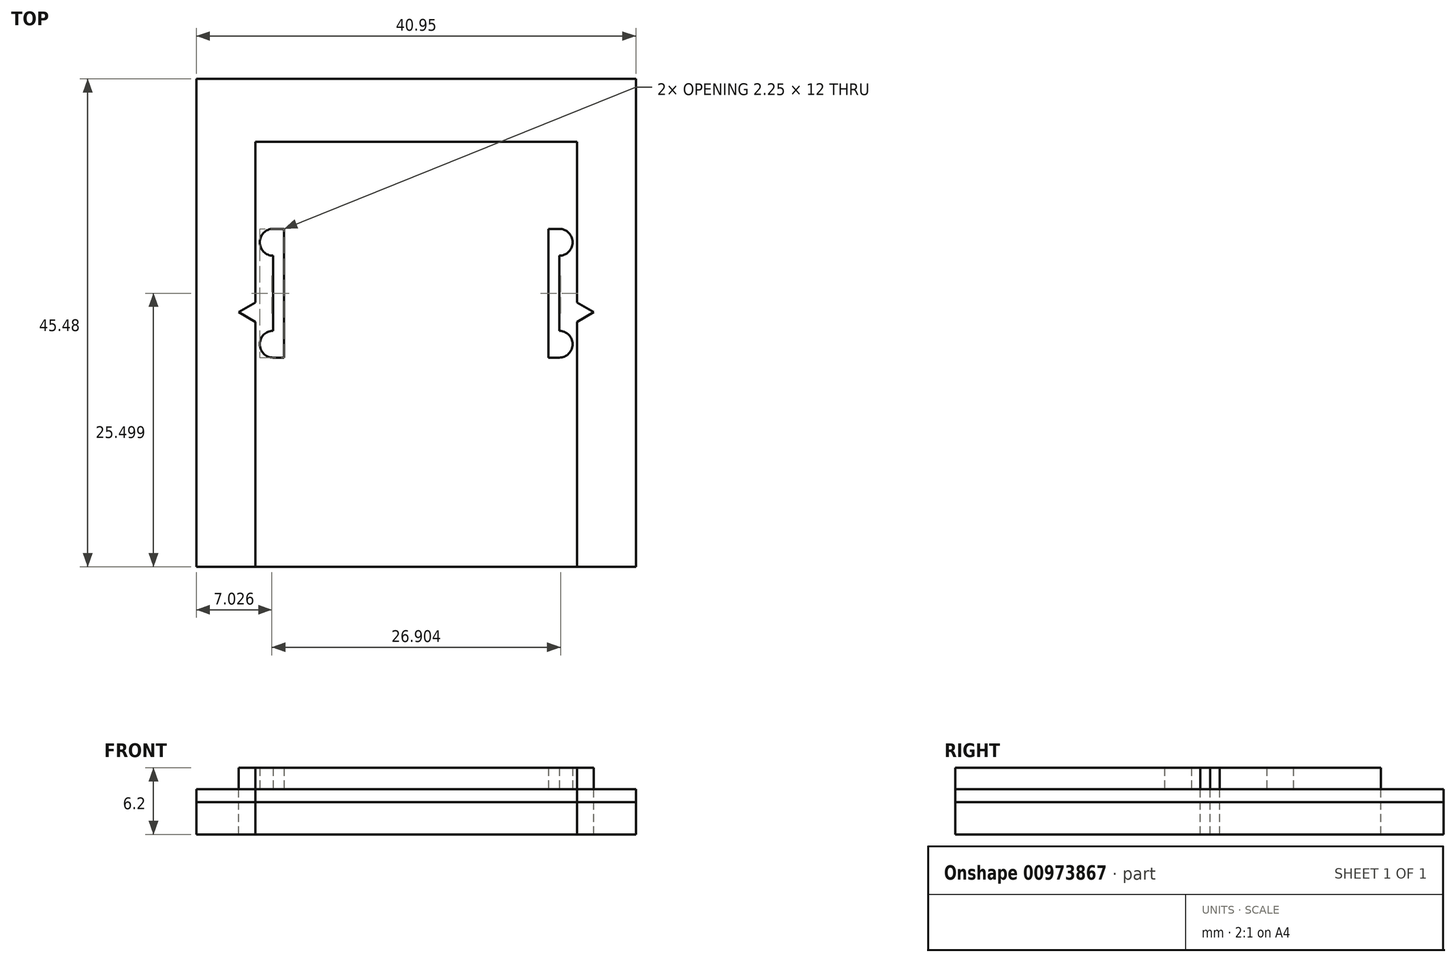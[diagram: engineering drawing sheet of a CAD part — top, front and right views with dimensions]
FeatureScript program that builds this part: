
annotation { "Feature Type Name" : "Feature", "Feature Type Description" : "" }
export const myFeature = defineFeature(function(context is Context, id is Id, definition is map)
    precondition{}
    {
        {
            var Q0;
            Q0=qCreatedBy(makeId("Top.planeOp"),FACE);
            var sketch = newSketch(context, id + "F0", { "sketchPlane" : qUnion([Q0])});
            skPoint(sketch, "E0.middle", {"position": v(-0.11, -0.1) * mm});
            skLineSegment(sketch, "E1.bottom", {"start": v(-15.6, -4.1) * mm, "end": v(-20.6, -4.1) * mm});
            skLineSegment(sketch, "E1.top", {"start": v(-15.6, 25.9) * mm, "end": v(-20.6, 25.9) * mm});
            skLineSegment(sketch, "E1.right", {"start": v(-20.6, -4.1) * mm, "end": v(-20.6, 25.9) * mm});
            skLineSegment(sketch, "E2.left", {"start": v(-15.6, 25.9) * mm, "end": v(-15.6, 20.9) * mm});
            skLineSegment(sketch, "E3.bottom", {"start": v(-13.45, 11.92) * mm, "end": v(-12.45, 11.92) * mm});
            skLineSegment(sketch, "E3.top", {"start": v(-13.45, -0.08) * mm, "end": v(-12.45, -0.08) * mm});
            skLineSegment(sketch, "E3.right", {"start": v(-12.45, 11.92) * mm, "end": v(-12.45, -0.08) * mm});
            skLineSegment(sketch, "E4", {"start": v(-13.45, 9.42) * mm, "end": v(-13.45, 2.42) * mm});
            skLineSegment(sketch, "E5", {"start": v(-15.1, 3.25) * mm, "end": v(-16.66, 4.15) * mm});
            skLineSegment(sketch, "E6", {"start": v(-16.66, 4.15) * mm, "end": v(-15.1, 5.05) * mm});
            skLineSegment(sketch, "E7", {"start": v(-15.6, 5.15) * mm, "end": v(-17.33, 4.15) * mm});
            skLineSegment(sketch, "E8", {"start": v(-17.33, 4.15) * mm, "end": v(-15.6, 3.15) * mm});
            skLineSegment(sketch, "E9", {"start": v(-15.6, -4.1) * mm, "end": v(-15.6, 3.15) * mm});
            skLineSegment(sketch, "E10", {"start": v(-15.6, 5.15) * mm, "end": v(-15.6, 20.9) * mm});
            skLineSegment(sketch, "E11", {"start": v(-15.1, 3.25) * mm, "end": v(-15.1, -19.58) * mm});
            skLineSegment(sketch, "E12", {"start": v(-15.1, 5.05) * mm, "end": v(-15.1, 20.05) * mm});
            skLineSegment(sketch, "E13", {"start": v(-0.12, 29.27) * mm, "end": v(-0.12, -29.21) * mm, "construction": true});
            skLineSegment(sketch, "E14", {"start": v(-15.6, 25.9) * mm, "end": v(-0.12, 25.9) * mm});
            skLineSegment(sketch, "E15", {"start": v(-15.6, 20.9) * mm, "end": v(-0.22, 20.9) * mm});
            skLineSegment(sketch, "E16", {"start": v(-15.1, 20.05) * mm, "end": v(-0.12, 20.05) * mm});
            skLineSegment(sketch, "E17", {"start": v(-15.1, -19.58) * mm, "end": v(-0.1, -19.58) * mm});
            skLineSegment(sketch, "E18.bottom", {"start": v(-20.6, 25.9) * mm, "end": v(0.3, 25.9) * mm});
            skLineSegment(sketch, "E18.top", {"start": v(-20.6, -19.58) * mm, "end": v(-0.1, -19.58) * mm});
            skLineSegment(sketch, "E18.left", {"start": v(-20.6, 25.9) * mm, "end": v(-20.6, -19.58) * mm});
            skLineSegment(sketch, "E19.MirrorCS", {"start": v(16.41, 4.15) * mm, "end": v(14.85, 5.05) * mm});
            skLineSegment(sketch, "E20.MirrorCS", {"start": v(14.85, 3.25) * mm, "end": v(16.41, 4.15) * mm});
            skLineSegment(sketch, "E21.MirrorCS", {"start": v(15.35, 5.15) * mm, "end": v(17.09, 4.15) * mm});
            skLineSegment(sketch, "E22.MirrorCS", {"start": v(13.2, -0.08) * mm, "end": v(12.2, -0.08) * mm});
            skLineSegment(sketch, "E23.MirrorCS", {"start": v(17.09, 4.15) * mm, "end": v(15.35, 3.15) * mm});
            skLineSegment(sketch, "E24.MirrorCS", {"start": v(13.2, 11.92) * mm, "end": v(12.2, 11.92) * mm});
            skLineSegment(sketch, "E25.MirrorCS", {"start": v(20.35, 25.9) * mm, "end": v(-0.54, 25.9) * mm});
            skLineSegment(sketch, "E26.MirrorCS", {"start": v(15.35, -4.1) * mm, "end": v(15.35, 3.15) * mm});
            skLineSegment(sketch, "E27.MirrorCS", {"start": v(14.85, 5.05) * mm, "end": v(14.85, 20.05) * mm});
            skLineSegment(sketch, "E28.MirrorCS", {"start": v(15.35, 25.9) * mm, "end": v(-0.12, 25.9) * mm});
            skLineSegment(sketch, "E29.MirrorCS", {"start": v(15.35, 25.9) * mm, "end": v(15.35, 20.9) * mm});
            skLineSegment(sketch, "E30.MirrorCS", {"start": v(15.35, 5.15) * mm, "end": v(15.35, 20.9) * mm});
            skLineSegment(sketch, "E31.MirrorCS", {"start": v(12.2, 11.92) * mm, "end": v(12.2, -0.08) * mm});
            skLineSegment(sketch, "E32.MirrorCS", {"start": v(20.35, -19.58) * mm, "end": v(-0.15, -19.58) * mm});
            skLineSegment(sketch, "E33.MirrorCS", {"start": v(20.35, 25.9) * mm, "end": v(20.35, -19.58) * mm});
            skLineSegment(sketch, "E34.MirrorCS", {"start": v(14.85, 3.25) * mm, "end": v(14.85, -19.58) * mm});
            skLineSegment(sketch, "E35.MirrorCS", {"start": v(15.35, 25.9) * mm, "end": v(20.35, 25.9) * mm});
            skPoint(sketch, "E36.MirrorP", {"position": v(-0.13, -0.1) * mm});
            skLineSegment(sketch, "E37.MirrorCS", {"start": v(15.35, 20.9) * mm, "end": v(-0.03, 20.9) * mm});
            skLineSegment(sketch, "E38.MirrorCS", {"start": v(15.35, -4.1) * mm, "end": v(20.35, -4.1) * mm});
            skLineSegment(sketch, "E39.MirrorCS", {"start": v(14.85, -19.58) * mm, "end": v(-0.15, -19.58) * mm});
            skLineSegment(sketch, "E40.MirrorCS", {"start": v(20.35, -4.1) * mm, "end": v(20.35, 25.9) * mm});
            skLineSegment(sketch, "E41.MirrorCS", {"start": v(14.85, 20.05) * mm, "end": v(-0.12, 20.05) * mm});
            skLineSegment(sketch, "E42.MirrorCS", {"start": v(13.2, 9.42) * mm, "end": v(13.2, 2.42) * mm});
            skArc(sketch, "E43", {"start": v(-13.45, 2.42) * mm, "mid": v(-14.7, 1.17) * mm, "end": v(-13.45, -0.08) * mm});
            skArc(sketch, "E44", {"start": v(-13.45, 11.92) * mm, "mid": v(-14.7, 10.67) * mm, "end": v(-13.45, 9.42) * mm});
            skArc(sketch, "E45", {"start": v(13.2, 9.42) * mm, "mid": v(14.45, 10.67) * mm, "end": v(13.2, 11.92) * mm});
            skArc(sketch, "E46", {"start": v(13.2, -0.08) * mm, "mid": v(14.45, 1.17) * mm, "end": v(13.2, 2.42) * mm});
            skSolve(sketch);
        }
        {
            var Q0;
            Q0=makeQuery(id+"F0.imprint","IMPRINT",FACE,{"disambiguationData":[TD([[makeQuery(id+"F0.imprint","IMPRINT",EDGE,{"derivedFrom":sQuery(id+"F0.wireOp",EDGE,"E3.bottom")}),1.0]])]});
            var Q1;
            Q1=makeQuery(id+"F0.imprint","IMPRINT",FACE,{"disambiguationData":[TD([[makeQuery(id+"F0.imprint","IMPRINT",EDGE,{"derivedFrom":sQuery(id+"F0.wireOp",EDGE,"E19.MirrorCS")}),1.0]])]});
            extrude(context, id + "F1", {"entities" : qUnion([Q0, Q1]), "depth" : 2 * mm, "offsetDistance" : 25 * mm});
        }
        {
            var Q0;
            {var subQ1=sQuery(id+"F0.wireOp",EDGE,"E1.bottom");Q0=makeQuery(id+"F0.imprint","IMPRINT",FACE,{"disambiguationData":[TD([[makeQuery(id+"F0.imprint","IMPRINT",EDGE,{"derivedFrom":subQ1}),-1.0]])]});}
            var Q1;
            {var subQ2=sQuery(id+"F0.wireOp",EDGE,"E2.left");Q1=makeQuery(id+"F0.imprint","IMPRINT",FACE,{"disambiguationData":[TD([[makeQuery(id+"F0.imprint","IMPRINT",EDGE,{"derivedFrom":subQ2}),1.0]])]});}
            var Q2;
            Q2=makeQuery(id+"F0.imprint","IMPRINT",FACE,{"disambiguationData":[TD([[makeQuery(id+"F0.imprint","IMPRINT",EDGE,{"derivedFrom":sQuery(id+"F0.wireOp",EDGE,"E21.MirrorCS")}),1.0]])]});
            extrude(context, id + "F2", {"entities" : qUnion([Q0, Q1, Q2]), "oppositeDirection" : true, "depth" : 4.2 * mm, "offsetDistance" : 25 * mm});
        }
        {
            var Q0;
            Q0=makeQuery(id+"F0.imprint","IMPRINT",FACE,{"disambiguationData":[TD([[makeQuery(id+"F0.imprint","IMPRINT",EDGE,{"derivedFrom":sQuery(id+"F0.wireOp",EDGE,"E21.MirrorCS")}),1.0]])]});
            var Q1;
            Q1=makeQuery(id+"F0.imprint","IMPRINT",FACE,{"disambiguationData":[TD([[makeQuery(id+"F0.imprint","IMPRINT",EDGE,{"derivedFrom":sQuery(id+"F0.wireOp",EDGE,"E3.bottom")}),1.0]])]});
            var Q2;
            {var subQ2=sQuery(id+"F0.wireOp",EDGE,"E2.left");Q2=makeQuery(id+"F0.imprint","IMPRINT",FACE,{"disambiguationData":[TD([[makeQuery(id+"F0.imprint","IMPRINT",EDGE,{"derivedFrom":subQ2}),1.0]])]});}
            var Q3;
            {var subQ1=sQuery(id+"F0.wireOp",EDGE,"E1.bottom");Q3=makeQuery(id+"F0.imprint","IMPRINT",FACE,{"disambiguationData":[TD([[makeQuery(id+"F0.imprint","IMPRINT",EDGE,{"derivedFrom":subQ1}),-1.0]])]});}
            var Q4;
            {var subQ1=sQuery(id+"F0.wireOp",EDGE,"E1.bottom");Q4=makeQuery(id+"F0.imprint","IMPRINT",FACE,{"disambiguationData":[TD([[makeQuery(id+"F0.imprint","IMPRINT",EDGE,{"derivedFrom":subQ1}),1.0]])]});}
            var Q5;
            Q5=makeQuery(id+"F0.imprint","IMPRINT",FACE,{"disambiguationData":[TD([[makeQuery(id+"F0.imprint","IMPRINT",EDGE,{"derivedFrom":sQuery(id+"F0.wireOp",EDGE,"E3.bottom")}),-1.0]])]});
            var Q6;
            Q6=makeQuery(id+"F0.imprint","IMPRINT",FACE,{"disambiguationData":[TD([[makeQuery(id+"F0.imprint","IMPRINT",EDGE,{"derivedFrom":sQuery(id+"F0.wireOp",EDGE,"E22.MirrorCS")}),-1.0]])]});
            extrude(context, id + "F3", {"entities" : qUnion([Q0, Q1, Q2, Q3, Q4, Q5, Q6]), "oppositeDirection" : true, "depth" : 1.2 * mm, "offsetDistance" : 25 * mm});
        }
    });
